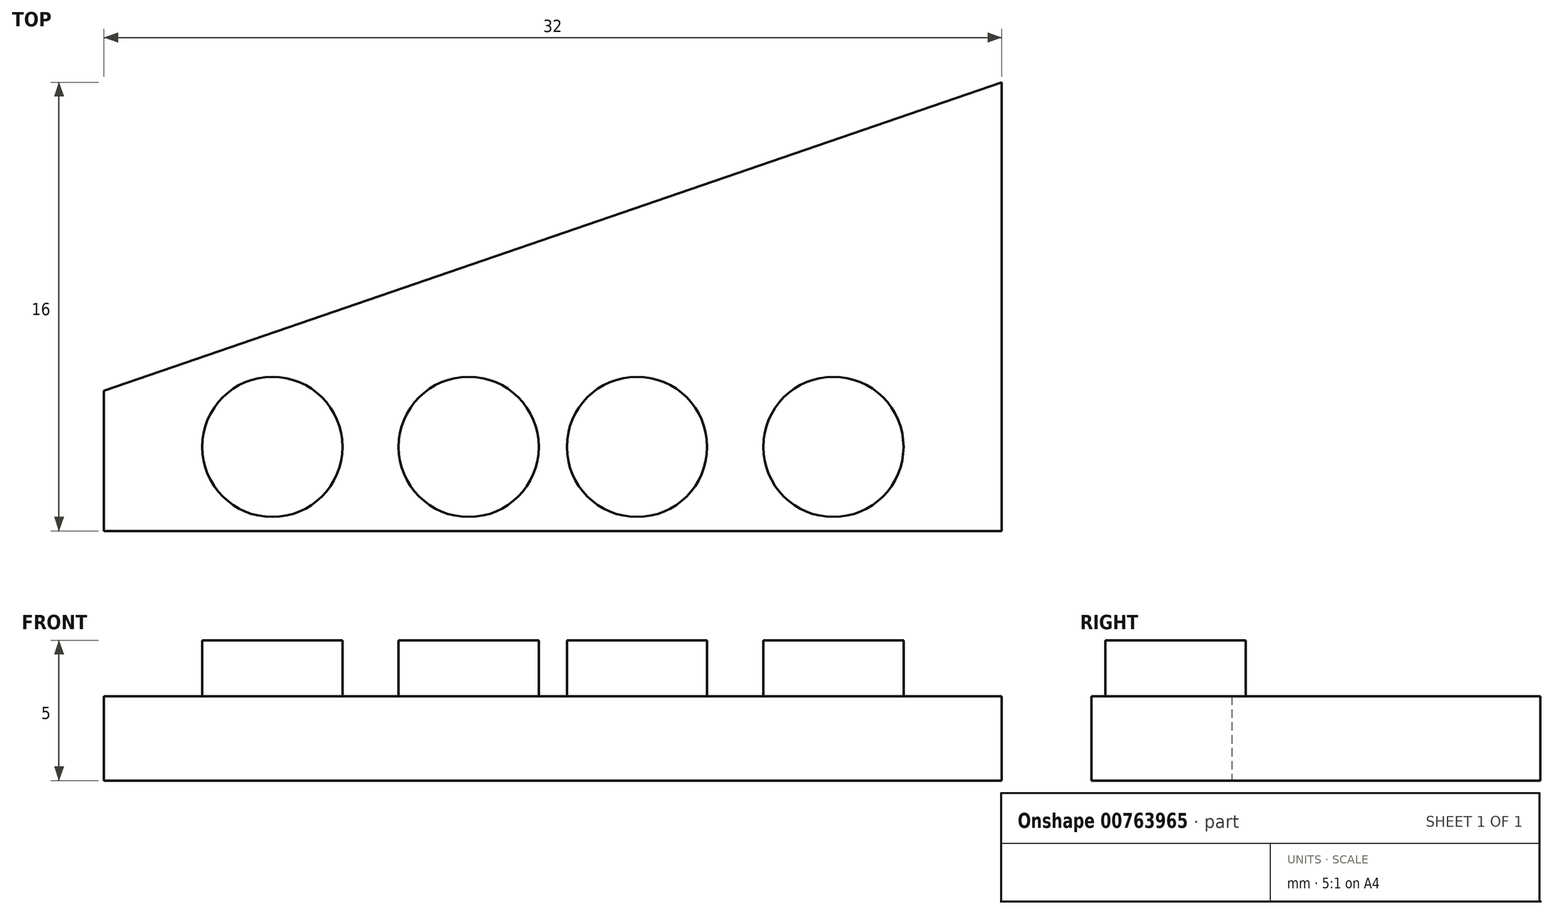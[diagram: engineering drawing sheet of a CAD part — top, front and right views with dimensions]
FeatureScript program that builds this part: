
annotation { "Feature Type Name" : "Feature", "Feature Type Description" : "" }
export const myFeature = defineFeature(function(context is Context, id is Id, definition is map)
    precondition{}
    {
        {
            var Q0;
            Q0=qCreatedBy(makeId("Top.planeOp"),FACE);
            var sketch = newSketch(context, id + "F0", { "sketchPlane" : qUnion([Q0])});
            skLineSegment(sketch, "E0.top", {"start": v(16, -8) * mm, "end": v(-16, -8) * mm});
            skLineSegment(sketch, "E0.left", {"start": v(16, 8) * mm, "end": v(16, -8) * mm});
            skLineSegment(sketch, "E0.right", {"start": v(-16, -3) * mm, "end": v(-16, -8) * mm});
            skPoint(sketch, "E0.middle", {"position": v(0, 0) * mm});
            skLineSegment(sketch, "E1", {"start": v(16, -8) * mm, "end": v(16, 8) * mm});
            skLineSegment(sketch, "E2", {"start": v(-16, -8) * mm, "end": v(-16, -3) * mm});
            skLineSegment(sketch, "E3", {"start": v(-16, -3) * mm, "end": v(16, 8) * mm});
            skSolve(sketch);
        }
        {
            var Q0;
            Q0 = qSketchRegion(id + "F0", true);
            extrude(context, id + "F1", {"entities" : qUnion([Q0]), "depth" : 3 * mm, "offsetDistance" : 25 * mm});
        }
        {
            var Q0;
            Q0=makeQuery(id+"F1.opExtrude","CAP_FACE",FACE,{"disambiguationData":[OSD([sQuery(id+"F0.wireOp",EDGE,"E0.top"),sQuery(id+"F0.wireOp",EDGE,"E1"),sQuery(id+"F0.wireOp",EDGE,"E2"),sQuery(id+"F0.wireOp",EDGE,"E3")])],"isStart":false});
            var sketch = newSketch(context, id + "F2", { "sketchPlane" : qUnion([Q0])});
            skCircle(sketch, "E4", {"center": v(10, -5) * mm, "radius": 2.5 * mm});
            skCircle(sketch, "E5", {"center": v(-10, -5) * mm, "radius": 2.5 * mm});
            skLineSegment(sketch, "E6", {"start": v(-16, -5) * mm, "end": v(16, -5) * mm});
            skPoint(sketch, "E7.center.orphan", {"position": v(-1.5, -5) * mm});
            skPoint(sketch, "E8.center.orphan", {"position": v(5.5, -5) * mm});
            skCircle(sketch, "E9", {"center": v(-3, -5) * mm, "radius": 2.5 * mm});
            skCircle(sketch, "E10", {"center": v(3, -5) * mm, "radius": 2.5 * mm});
            skSolve(sketch);
        }
        {
            var Q0;
            Q0=makeQuery(id+"F2.imprint","IMPRINT",FACE,{"disambiguationData":[TD([[makeQuery(id+"F2.imprint","IMPRINT",EDGE,{"derivedFrom":sQuery(id+"F2.wireOp",EDGE,"E8")}),1.0]])]});
            var Q1;
            Q1=makeQuery(id+"F2.imprint","IMPRINT",FACE,{"disambiguationData":[TD([[makeQuery(id+"F2.imprint","IMPRINT",EDGE,{"derivedFrom":sQuery(id+"F2.wireOp",EDGE,"E4")}),1.0]])]});
            var Q2;
            Q2=makeQuery(id+"F2.imprint","IMPRINT",FACE,{"disambiguationData":[TD([[makeQuery(id+"F2.imprint","IMPRINT",EDGE,{"derivedFrom":sQuery(id+"F2.wireOp",EDGE,"E7")}),1.0]])]});
            var Q3;
            Q3=makeQuery(id+"F2.imprint","IMPRINT",FACE,{"disambiguationData":[TD([[makeQuery(id+"F2.imprint","IMPRINT",EDGE,{"derivedFrom":sQuery(id+"F2.wireOp",EDGE,"E5")}),1.0]])]});
            extrude(context, id + "F3", {"entities" : qUnion([Q0, Q1, Q2, Q3]), "operationType" : NewBodyOperationType.ADD, "depth" : 2 * mm, "offsetDistance" : 25 * mm});
        }
        {
            var Q0;
            Q0 = qSketchRegion(id + "F2", true);
            extrude(context, id + "F4", {"entities" : qUnion([Q0]), "operationType" : NewBodyOperationType.ADD, "depth" : 2 * mm, "offsetDistance" : 25 * mm});
        }
    });
